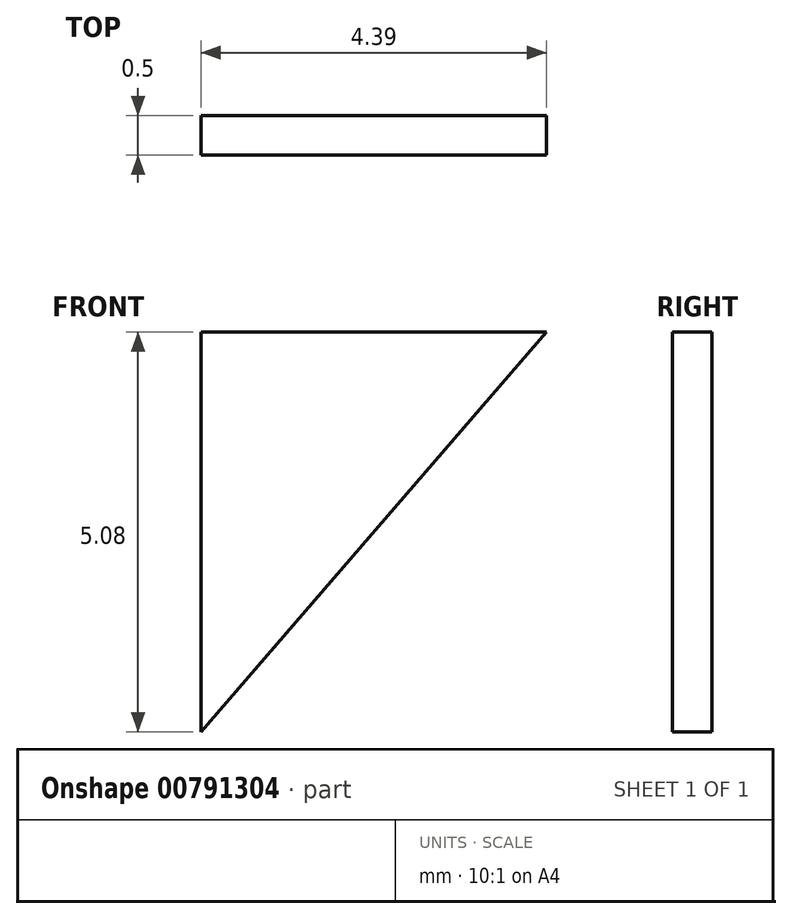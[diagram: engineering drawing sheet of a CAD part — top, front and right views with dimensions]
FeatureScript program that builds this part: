
annotation { "Feature Type Name" : "Feature", "Feature Type Description" : "" }
export const myFeature = defineFeature(function(context is Context, id is Id, definition is map)
    precondition{}
    {
        {
            var Q0;
            Q0=qCreatedBy(makeId("Front.planeOp"),FACE);
            var sketch = newSketch(context, id + "F0", { "sketchPlane" : qUnion([Q0])});
            skLineSegment(sketch, "E0", {"start": v(-55.47, 42.24) * mm, "end": v(-55.47, 37.16) * mm});
            skLineSegment(sketch, "E1", {"start": v(-55.47, 37.16) * mm, "end": v(-51.08, 42.24) * mm});
            skLineSegment(sketch, "E2", {"start": v(-51.08, 42.24) * mm, "end": v(-55.47, 42.24) * mm});
            skSolve(sketch);
        }
        {
            var Q0;
            Q0 = qSketchRegion(id + "F0", true);
            extrude(context, id + "F1", {"entities" : qUnion([Q0]), "depth" : .5 * mm, "offsetDistance" : 25.4 * mm});
        }
    });
